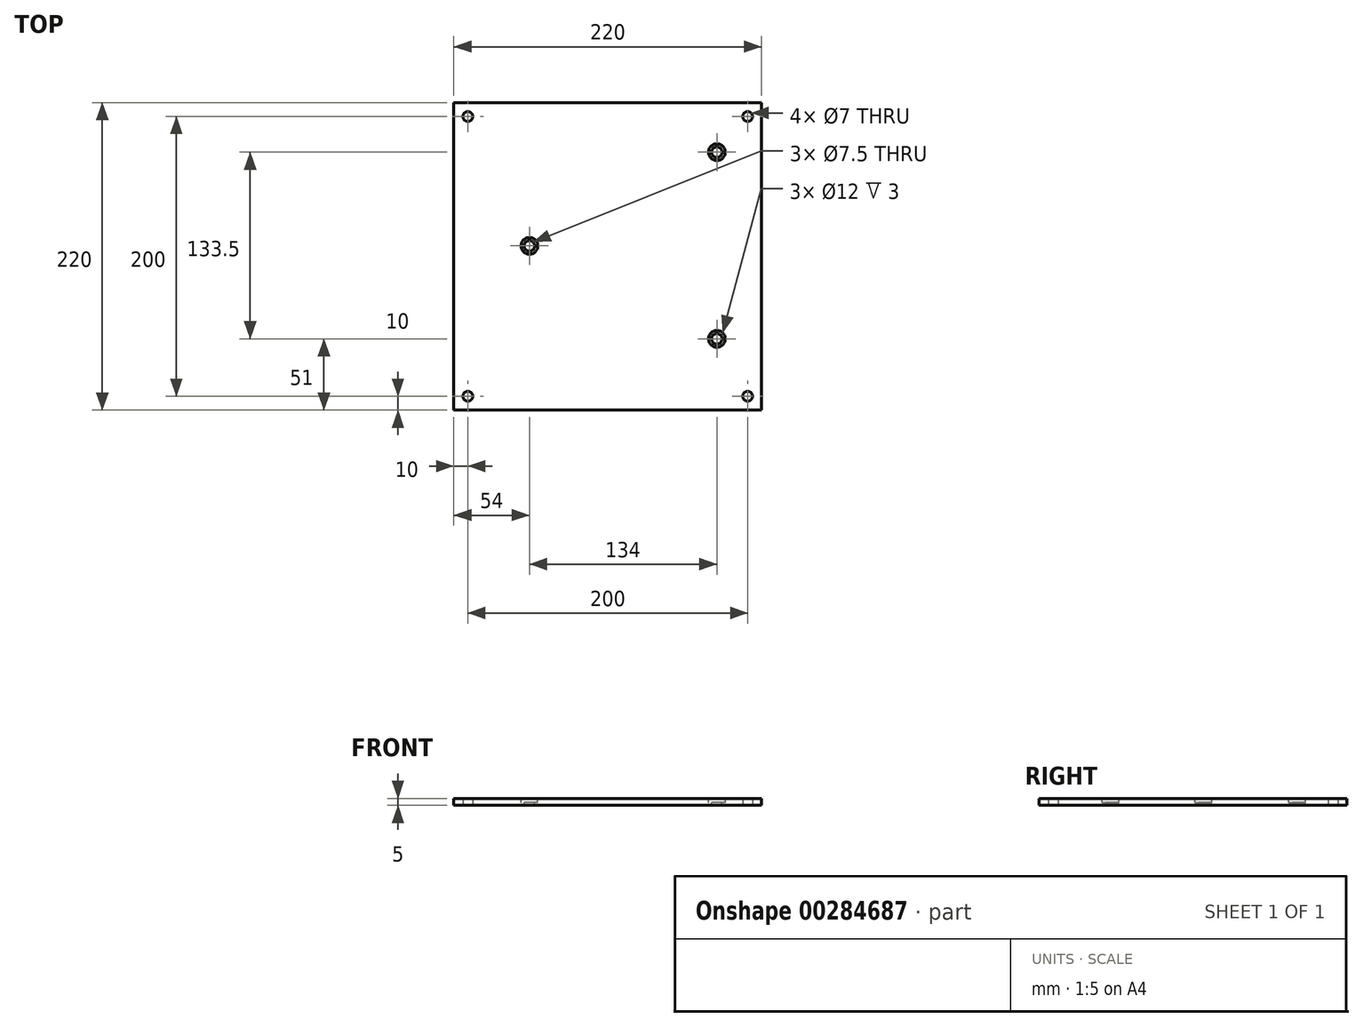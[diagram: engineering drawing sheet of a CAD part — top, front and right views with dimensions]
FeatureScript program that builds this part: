
annotation { "Feature Type Name" : "Feature", "Feature Type Description" : "" }
export const myFeature = defineFeature(function(context is Context, id is Id, definition is map)
    precondition{}
    {
        {
            var Q0;
            Q0=qCreatedBy(makeId("Top.planeOp"),FACE);
            var sketch = newSketch(context, id + "F0", { "sketchPlane" : qUnion([Q0])});
            skLineSegment(sketch, "E0.bottom", {"start": v(-110, 110) * mm, "end": v(110, 110) * mm});
            skLineSegment(sketch, "E0.top", {"start": v(-110, -110) * mm, "end": v(110, -110) * mm});
            skLineSegment(sketch, "E0.left", {"start": v(-110, 110) * mm, "end": v(-110, -110) * mm});
            skLineSegment(sketch, "E0.right", {"start": v(110, 110) * mm, "end": v(110, -110) * mm});
            skCircle(sketch, "E1", {"center": v(-100, 100) * mm, "radius": 3.5 * mm});
            skCircle(sketch, "E2", {"center": v(-100, -100) * mm, "radius": 3.5 * mm});
            skCircle(sketch, "E3", {"center": v(100, -100) * mm, "radius": 3.5 * mm});
            skCircle(sketch, "E4", {"center": v(100, 100) * mm, "radius": 3.5 * mm});
            skSolve(sketch);
        }
        {
            var Q0;
            Q0 = qSketchRegion(id + "F0", true);
            extrude(context, id + "F1", {"entities" : qUnion([Q0]), "depth" : 5 * mm});
        }
        {
            var Q0;
            Q0=makeQuery(id+"F1.opExtrude","CAP_FACE",FACE,{"disambiguationData":[OSD([sQuery(id+"F0.wireOp",EDGE,"E0.bottom"),sQuery(id+"F0.wireOp",EDGE,"E0.top"),sQuery(id+"F0.wireOp",EDGE,"E0.left"),sQuery(id+"F0.wireOp",EDGE,"E0.right"),sQuery(id+"F0.wireOp",EDGE,"E1"),sQuery(id+"F0.wireOp",EDGE,"E2"),sQuery(id+"F0.wireOp",EDGE,"E3"),sQuery(id+"F0.wireOp",EDGE,"E4")])],"isStart":false});
            var sketch = newSketch(context, id + "F2", { "sketchPlane" : qUnion([Q0])});
            skCircle(sketch, "E5", {"center": v(-56, 7.5) * mm, "radius": 3.75 * mm});
            skCircle(sketch, "E6", {"center": v(78, 74.5) * mm, "radius": 3.75 * mm});
            skCircle(sketch, "E7", {"center": v(78, -59) * mm, "radius": 3.75 * mm});
            skSolve(sketch);
        }
        {
            var Q0;
            Q0 = qSketchRegion(id + "F2", true);
            extrude(context, id + "F3", {"entities" : qUnion([Q0]), "operationType" : NewBodyOperationType.REMOVE, "endBound" : BoundingType.THROUGH_ALL, "oppositeDirection" : true, "depth" : 25 * mm});
        }
        {
            var Q0;
            Q0=makeQuery(id+"F1.opExtrude","CAP_FACE",FACE,{"disambiguationData":[OSD([sQuery(id+"F0.wireOp",EDGE,"E0.bottom"),sQuery(id+"F0.wireOp",EDGE,"E0.top"),sQuery(id+"F0.wireOp",EDGE,"E0.left"),sQuery(id+"F0.wireOp",EDGE,"E0.right"),sQuery(id+"F0.wireOp",EDGE,"E1"),sQuery(id+"F0.wireOp",EDGE,"E2"),sQuery(id+"F0.wireOp",EDGE,"E3"),sQuery(id+"F0.wireOp",EDGE,"E4")])],"isStart":false});
            var sketch = newSketch(context, id + "F4", { "sketchPlane" : qUnion([Q0])});
            skCircle(sketch, "E8", {"center": v(-56, 7.5) * mm, "radius": 6 * mm});
            skCircle(sketch, "E9", {"center": v(78, 74.5) * mm, "radius": 6 * mm});
            skCircle(sketch, "E10", {"center": v(78, -59) * mm, "radius": 6 * mm});
            skSolve(sketch);
        }
        {
            var Q0;
            Q0 = qSketchRegion(id + "F4", true);
            extrude(context, id + "F5", {"entities" : qUnion([Q0]), "operationType" : NewBodyOperationType.REMOVE, "oppositeDirection" : true, "depth" : 3 * mm});
        }
    });
